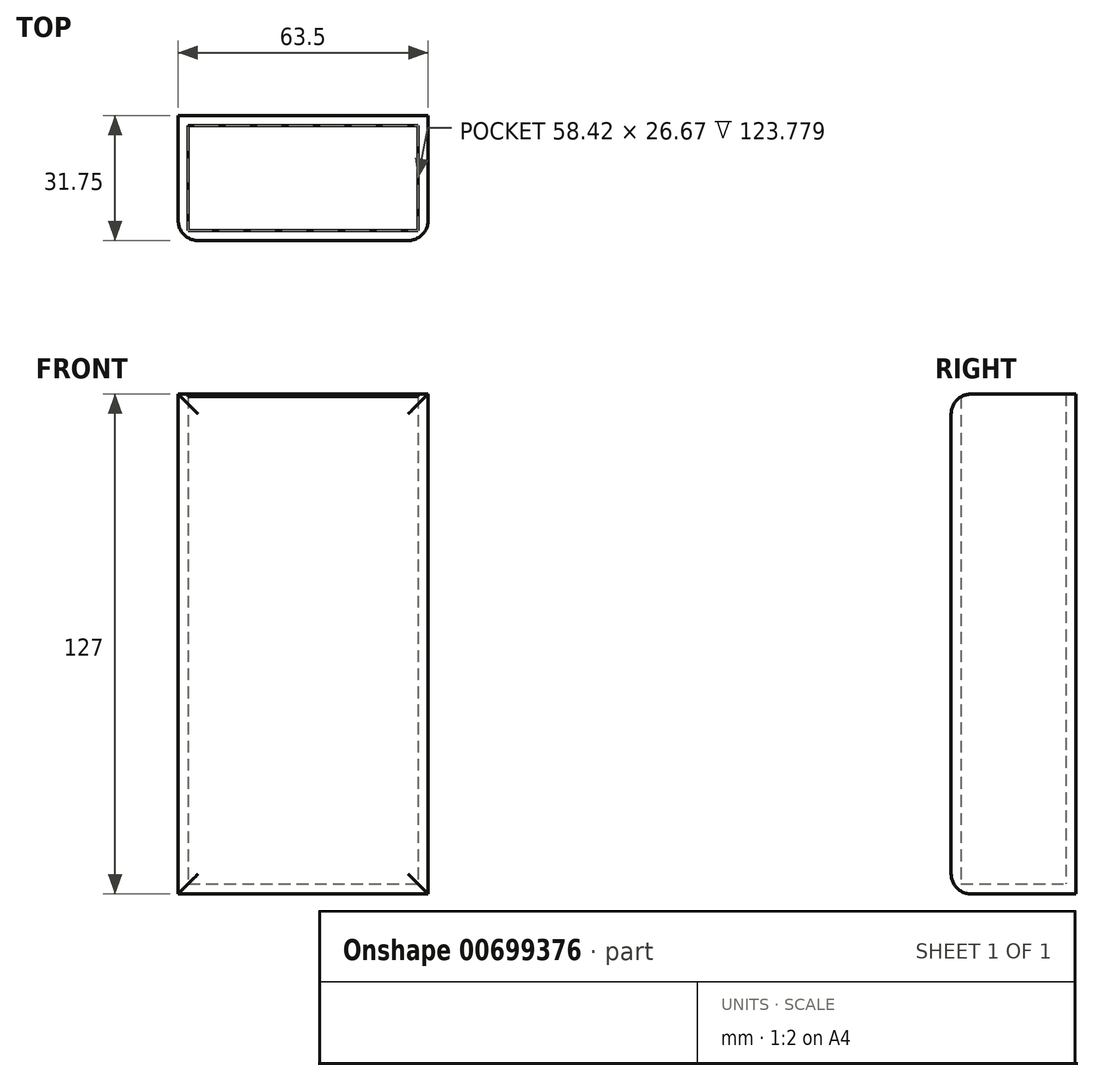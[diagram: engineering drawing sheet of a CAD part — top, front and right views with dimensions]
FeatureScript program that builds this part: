
annotation { "Feature Type Name" : "Feature", "Feature Type Description" : "" }
export const myFeature = defineFeature(function(context is Context, id is Id, definition is map)
    precondition{}
    {
        {
            var Q0;
            Q0=qCreatedBy(makeId("Front.planeOp"),FACE);
            var sketch = newSketch(context, id + "F0", { "sketchPlane" : qUnion([Q0])});
            skLineSegment(sketch, "E0.bottom", {"start": v(-31.75, 63.5) * mm, "end": v(31.75, 63.5) * mm});
            skLineSegment(sketch, "E0.top", {"start": v(-31.75, -63.5) * mm, "end": v(31.75, -63.5) * mm});
            skLineSegment(sketch, "E0.left", {"start": v(-31.75, 63.5) * mm, "end": v(-31.75, -63.5) * mm});
            skLineSegment(sketch, "E0.right", {"start": v(31.75, 63.5) * mm, "end": v(31.75, -63.5) * mm});
            skPoint(sketch, "E0.middle", {"position": v(0, 0) * mm});
            skSolve(sketch);
        }
        {
            var Q0;
            Q0=makeQuery(id+"F0.imprint","IMPRINT",FACE,{"disambiguationData":[TD([[makeQuery(id+"F0.imprint","IMPRINT",EDGE,{"derivedFrom":sQuery(id+"F0.wireOp",EDGE,"E0.bottom")}),-1.0]])]});
            extrude(context, id + "F1", {"entities" : qUnion([Q0]), "depth" : 31.75 * mm, "offsetDistance" : 25.4 * mm});
        }
        {
            var Q0;
            Q0=makeQuery(id+"F1.opExtrude","SWEPT_FACE",FACE,{"disambiguationData":[OSD([sQuery(id+"F0.wireOp",EDGE,"E0.bottom")])]});
            shell(context, id + "F2", {"entities" : qUnion([Q0]), "thickness" : 2.54 * mm});
        }
        {
            var Q0;
            Q0=makeQuery(id+"F1.opExtrude","CAP_FACE",FACE,{"disambiguationData":[OSD([sQuery(id+"F0.wireOp",EDGE,"E0.bottom"),sQuery(id+"F0.wireOp",EDGE,"E0.top"),sQuery(id+"F0.wireOp",EDGE,"E0.left"),sQuery(id+"F0.wireOp",EDGE,"E0.right")])],"isStart":false});
            fillet(context, id + "F3", {"entities" : qUnion([Q0]), "radius" : 5.08 * mm, "tangentPropagation" : true, "allowEdgeOverflow" : false});
        }
    });
